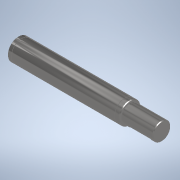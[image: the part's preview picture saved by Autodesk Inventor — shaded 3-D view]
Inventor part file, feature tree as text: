
AUTODESK INVENTOR PART (.ipt)
format: ipt  version: 2021.3 (Build 253353000, 353)  size: 186,368 bytes
history: native  units: mm (DEFAULTED — no unit token found)
features: other x14, sketch x7, revolve x4, extrude x3
ambient origin geometry x8: Origin, YZ Plane, XZ Plane, XY Plane, X Axis, Y Axis, Z Axis, Center Point
bodies: Solid1 (feature_tree)
feature tree (28):
  revolve  "Revolution1"  Angle=360.0deg
  revolve  "Revolution2"  Angle=360.0deg
  revolve  "Revolution3"  [1 undecoded]
  revolve  "Revolution4"  [1 undecoded]
  extrude  "Extrusion1"  [1 undecoded]
  extrude  "Extrusion2"  [1 undecoded]
  extrude  "Extrusion3"  [1 undecoded]
  other  "to_c_ring_2_XY"
  other  "to_c_ring_2_YZ"
  other  "to_c_ring_2_ZX"
  other  "to_c_ring_2_X"
  other  "to_c_ring_2_Y"
  other  "to_c_ring_2_Z"
  other  "to_c_ring_2_Center"
  other  "to_c_ring_3_XY"
  other  "to_c_ring_3_YZ"
  other  "to_c_ring_3_ZX"
  other  "to_c_ring_3_X"
  other  "to_c_ring_3_Y"
  other  "to_c_ring_3_Z"
  other  "to_c_ring_3_Center"
  sketch  "Sketch_1"  dims[d0=360.0deg d1=360.0deg]
  sketch  "Sketch_2"  dims[d2=360.0deg d3=360.0deg]
  sketch  "Sketch_15"  dims[d4=3.0mm d5=0.0mm d6=3.0mm d7=0.0mm]
  sketch  "Sketch_16"  dims[d8=18.0mm d9=0.0mm]
  sketch  "Sketch_20"
  sketch  "Sketch_21"
  sketch  "Sketch_63"
note: 5 required parameter values undecoded (feature->parameter linkage not recoverable at this tier; creation-order binding heuristic only, values carry confidence <= 0.55)